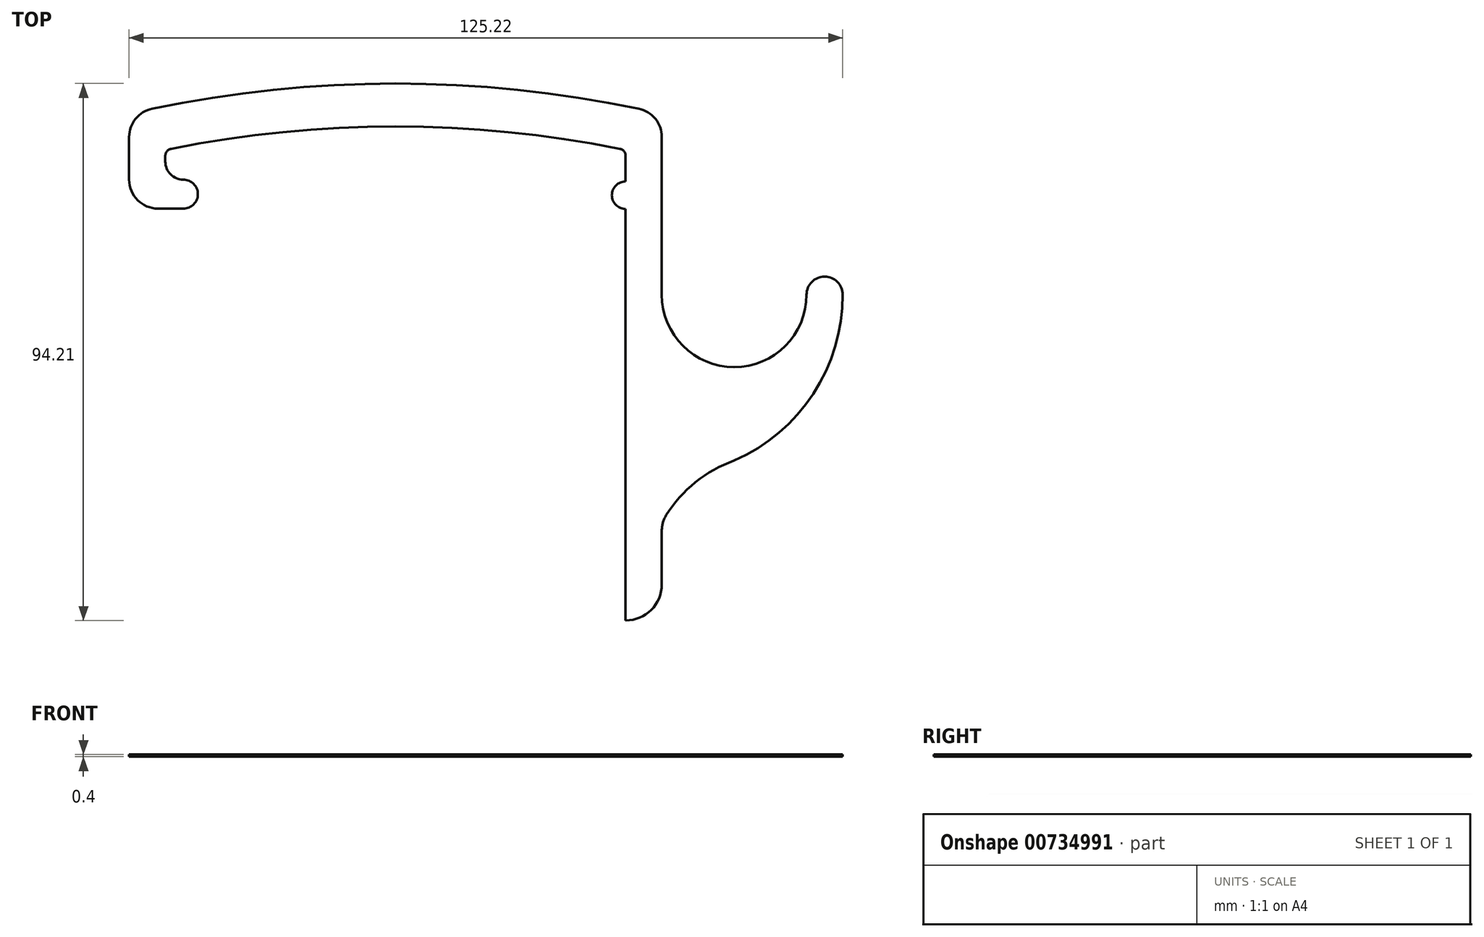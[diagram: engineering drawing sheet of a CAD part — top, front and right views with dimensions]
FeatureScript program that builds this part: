
annotation { "Feature Type Name" : "Feature", "Feature Type Description" : "" }
export const myFeature = defineFeature(function(context is Context, id is Id, definition is map)
    precondition{}
    {
        {
            assignVariable(context, id + "F0", {"name" : "THICKNESS", "anyValue" : .4});
        }
        {
            var Q0;
            Q0=qCreatedBy(makeId("Top.planeOp"),FACE);
            var sketch = newSketch(context, id + "F1", { "sketchPlane" : qUnion([Q0])});
            skLineSegment(sketch, "E0", {"start": v(0, -76.2) * mm, "end": v(0, 0) * mm});
            skLineSegment(sketch, "E1", {"start": v(-40.39, -196.85) * mm, "end": v(-40.39, 86.17) * mm, "construction": true});
            skArc(sketch, "E2", {"start": v(0, 0) * mm, "mid": v(-20.09, 3.07) * mm, "end": v(-40.39, 4.1) * mm});
            skArc(sketch, "E3.MirrorCS", {"start": v(-80.77, 0) * mm, "mid": v(-60.68, 3.07) * mm, "end": v(-40.39, 4.1) * mm});
            skLineSegment(sketch, "E4", {"start": v(0, -76.2) * mm, "end": v(6.35, -76.2) * mm});
            skLineSegment(sketch, "E5", {"start": v(6.35, -76.2) * mm, "end": v(6.35, 6.35) * mm});
            skLineSegment(sketch, "E6", {"start": v(-80.77, 0) * mm, "end": v(-80.77, -2.03) * mm});
            skArc(sketch, "E7", {"start": v(-80.77, -2.03) * mm, "mid": v(-79.84, -4.28) * mm, "end": v(-77.6, -5.2) * mm});
            skArc(sketch, "E8", {"start": v(-77.6, -5.2) * mm, "mid": v(-75.06, -7.75) * mm, "end": v(-77.6, -10.29) * mm});
            skArc(sketch, "E9", {"start": v(6.35, 6.35) * mm, "mid": v(-16.87, 10.32) * mm, "end": v(-40.39, 11.66) * mm});
            skArc(sketch, "E10.MirrorCS", {"start": v(-87.12, 6.35) * mm, "mid": v(-63.9, 10.32) * mm, "end": v(-40.39, 11.66) * mm});
            skLineSegment(sketch, "E11", {"start": v(-87.12, 6.35) * mm, "end": v(-87.12, -10.29) * mm});
            skArc(sketch, "E12", {"start": v(6.35, -76.2) * mm, "mid": v(4.5, -80.7) * mm, "end": v(0, -82.55) * mm});
            skLineSegment(sketch, "E13", {"start": v(0, -76.2) * mm, "end": v(0, -82.55) * mm});
            skLineSegment(sketch, "E14", {"start": v(-77.6, -10.29) * mm, "end": v(-87.12, -10.29) * mm});
            skSolve(sketch);
        }
        {
            var Q0;
            Q0 = qSketchRegion(id + "F1", true);
            extrude(context, id + "F2", {"entities" : qUnion([Q0]), "depth" : (getVariable(context, 'THICKNESS')) * mm, "offsetDistance" : 25.4 * mm});
        }
        {
            var Q0;
            Q0=qCreatedBy(makeId("Top.planeOp"),FACE);
            var sketch = newSketch(context, id + "F3", { "sketchPlane" : qUnion([Q0])});
            skCircle(sketch, "E15", {"center": v(0, -7.94) * mm, "radius": 2.41 * mm});
            skSolve(sketch);
        }
        {
            var Q0;
            Q0=qSketchRegion(id+"F3",true);
            extrude(context, id + "F4", {"entities" : qUnion([Q0]), "operationType" : NewBodyOperationType.ADD, "depth" : (getVariable(context, 'THICKNESS')) * mm, "offsetDistance" : 25.4 * mm});
        }
        {
            var Q0;
            Q0=makeQuery(id+"F2.opExtrude","SWEPT_EDGE",EDGE,{"disambiguationData":[OSD([sQuery(id+"F1.wireOp",EDGE,"E10.MirrorCS"),sQuery(id+"F1.wireOp",EDGE,"E11")])]});
            var Q1;
            Q1=makeQuery(id+"F2.opExtrude","SWEPT_EDGE",EDGE,{"disambiguationData":[OSD([sQuery(id+"F1.wireOp",EDGE,"E5"),sQuery(id+"F1.wireOp",EDGE,"E9")])]});
            var Q2;
            Q2=makeQuery(id+"F2.opExtrude","SWEPT_EDGE",EDGE,{"disambiguationData":[OSD([sQuery(id+"F1.wireOp",EDGE,"E11"),sQuery(id+"F1.wireOp",EDGE,"nPjlojTF-CVGx-MTEt-pRxP-OlM7tPyFeRFX")])]});
            fillet(context, id + "F5", {"entities" : qUnion([Q0, Q1, Q2]), "radius" : 5.08 * mm, "tangentPropagation" : true, "allowEdgeOverflow" : false});
        }
        {
            var Q0;
            Q0=makeQuery(id+"F2.opExtrude","SWEPT_EDGE",EDGE,{"disambiguationData":[OSD([sQuery(id+"F1.wireOp",EDGE,"E0"),sQuery(id+"F1.wireOp",EDGE,"E2")])]});
            var Q1;
            Q1=makeQuery(id+"F2.opExtrude","SWEPT_EDGE",EDGE,{"disambiguationData":[OSD([sQuery(id+"F1.wireOp",EDGE,"E3.MirrorCS"),sQuery(id+"F1.wireOp",EDGE,"E6")])]});
            fillet(context, id + "F6", {"entities" : qUnion([Q0, Q1]), "radius" : 1.27 * mm, "tangentPropagation" : true, "allowEdgeOverflow" : false});
        }
        {
            var Q0;
            Q0=qCreatedBy(makeId("Top.planeOp"),FACE);
            var sketch = newSketch(context, id + "F7", { "sketchPlane" : qUnion([Q0])});
            skArc(sketch, "E16", {"start": v(6.35, -25.4) * mm, "mid": v(19.05, -38.1) * mm, "end": v(31.75, -25.4) * mm});
            skLineSegment(sketch, "E17", {"start": v(-17.7, -25.4) * mm, "end": v(46.73, -25.4) * mm, "construction": true});
            skCircle(sketch, "E18", {"center": v(34.92, -25.4) * mm, "radius": 3.18 * mm});
            skLineSegment(sketch, "E19", {"start": v(19.05, -25.4) * mm, "end": v(19.05, -101.6) * mm, "construction": true});
            skLineSegment(sketch, "E20", {"start": v(26.67, -25.4) * mm, "end": v(26.67, -101.6) * mm, "construction": true});
            skArc(sketch, "E21", {"start": v(38.1, -25.4) * mm, "mid": v(32.91, -42.8) * mm, "end": v(19.05, -54.5) * mm});
            skArc(sketch, "E22", {"start": v(19.05, -54.5) * mm, "mid": v(11.67, -58.77) * mm, "end": v(6.35, -65.43) * mm});
            skLineSegment(sketch, "E23", {"start": v(6.35, -25.4) * mm, "end": v(6.35, -65.43) * mm});
            skSolve(sketch);
        }
        {
            var Q0;
            Q0=qSketchRegion(id+"F7",true);
            extrude(context, id + "F8", {"entities" : qUnion([Q0]), "operationType" : NewBodyOperationType.ADD, "depth" : (getVariable(context, 'THICKNESS')) * mm, "offsetDistance" : 25.4 * mm});
        }
        {
            var Q0;
            Q0=makeQuery(id+"F8.opExtrude","SWEPT_EDGE",EDGE,{"disambiguationData":[OSD([sQuery(id+"F7.wireOp",EDGE,"E22"),sQuery(id+"F7.wireOp",EDGE,"E23")])]});
            fillet(context, id + "F9", {"entities" : qUnion([Q0]), "radius" : 5.08 * mm, "tangentPropagation" : true, "allowEdgeOverflow" : false});
        }
    });
